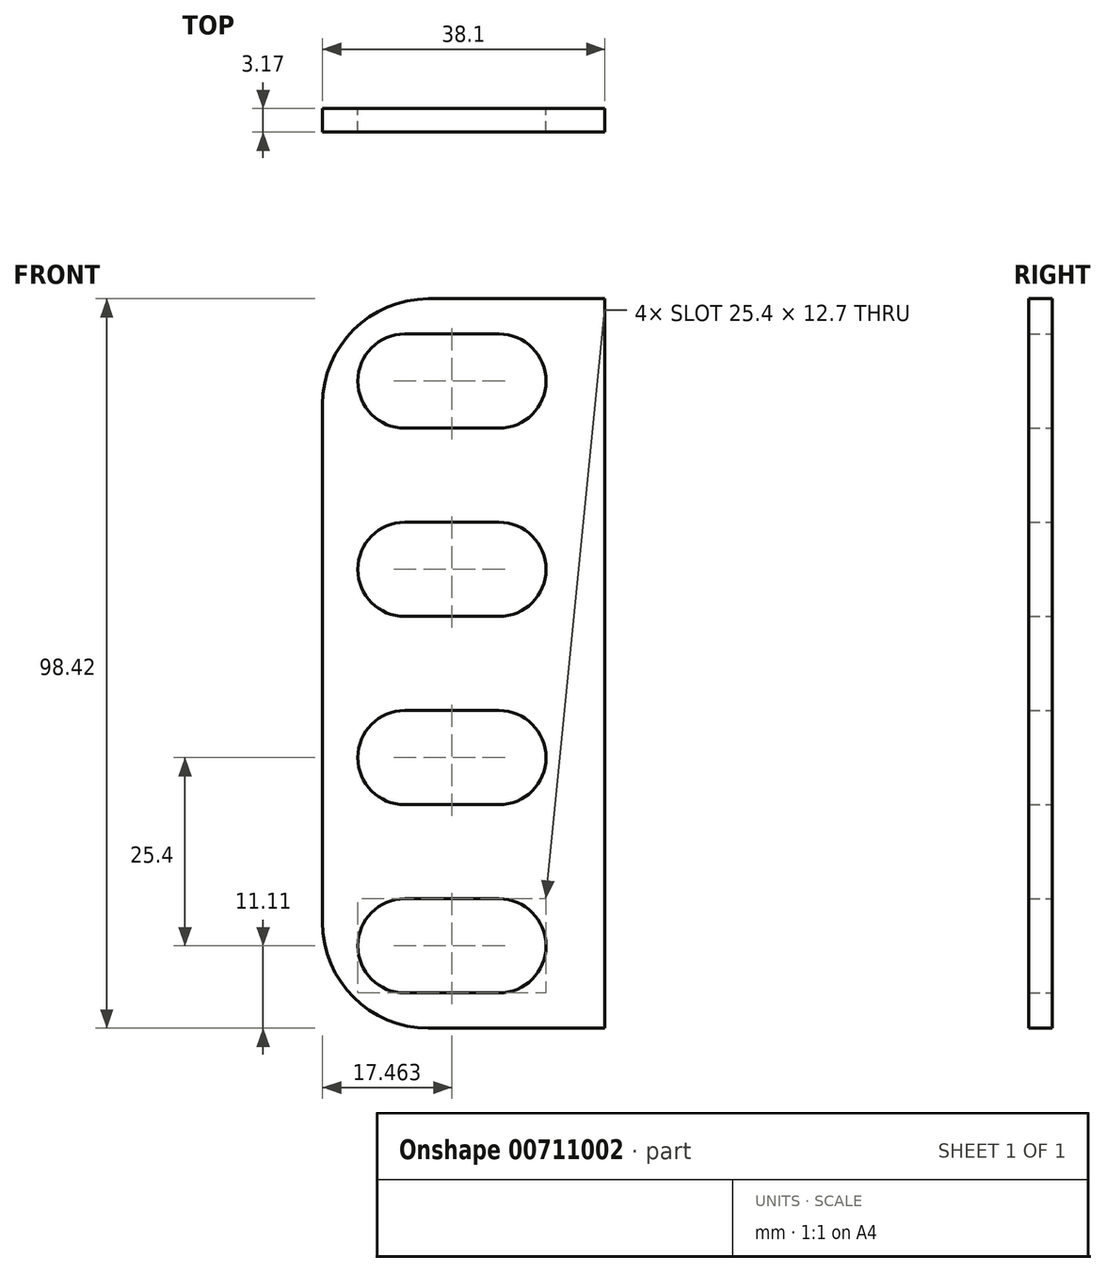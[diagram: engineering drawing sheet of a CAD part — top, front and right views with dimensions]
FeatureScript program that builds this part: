
annotation { "Feature Type Name" : "Feature", "Feature Type Description" : "" }
export const myFeature = defineFeature(function(context is Context, id is Id, definition is map)
    precondition{}
    {
        {
            var Q0;
            Q0=qCreatedBy(makeId("Front.planeOp"),FACE);
            var sketch = newSketch(context, id + "F0", { "sketchPlane" : qUnion([Q0])});
            skLineSegment(sketch, "E0.bottom", {"start": v(19.05, -49.21) * mm, "end": v(-4.76, -49.21) * mm});
            skLineSegment(sketch, "E0.top", {"start": v(19.05, 49.21) * mm, "end": v(-4.76, 49.21) * mm});
            skLineSegment(sketch, "E0.left", {"start": v(19.05, -49.21) * mm, "end": v(19.05, 49.21) * mm});
            skLineSegment(sketch, "E0.right", {"start": v(-19.05, -34.93) * mm, "end": v(-19.05, 34.92) * mm});
            skPoint(sketch, "E0.middle", {"position": v(0, 0) * mm});
            skPoint(sketch, "E1.visualSharp", {"position": v(-19.05, 49.21) * mm});
            skArc(sketch, "E1.filletArc", {"start": v(-4.76, 49.21) * mm, "mid": v(-14.87, 45.03) * mm, "end": v(-19.05, 34.92) * mm});
            skPoint(sketch, "E2.visualSharp", {"position": v(-19.05, -49.21) * mm});
            skArc(sketch, "E2.filletArc", {"start": v(-19.05, -34.93) * mm, "mid": v(-14.87, -45.03) * mm, "end": v(-4.76, -49.21) * mm});
            skLineSegment(sketch, "E3.bottom", {"start": v(4.76, -44.45) * mm, "end": v(-7.94, -44.45) * mm});
            skLineSegment(sketch, "E3.top", {"start": v(4.76, -31.75) * mm, "end": v(-7.94, -31.75) * mm});
            skLineSegment(sketch, "E3.left", {"start": v(11.11, -38.1) * mm, "end": v(11.11, -38.1) * mm});
            skLineSegment(sketch, "E3.right", {"start": v(-14.29, -38.1) * mm, "end": v(-14.29, -38.1) * mm});
            skPoint(sketch, "E4.visualSharp", {"position": v(-14.29, -31.75) * mm});
            skArc(sketch, "E4.filletArc", {"start": v(-7.94, -31.75) * mm, "mid": v(-12.43, -33.6) * mm, "end": v(-14.29, -38.1) * mm});
            skPoint(sketch, "E5.visualSharp", {"position": v(-14.29, -44.45) * mm});
            skArc(sketch, "E5.filletArc", {"start": v(-14.29, -38.1) * mm, "mid": v(-12.43, -42.6) * mm, "end": v(-7.94, -44.45) * mm});
            skPoint(sketch, "E6.visualSharp", {"position": v(11.11, -31.75) * mm});
            skArc(sketch, "E6.filletArc", {"start": v(11.11, -38.1) * mm, "mid": v(9.25, -33.6) * mm, "end": v(4.76, -31.75) * mm});
            skPoint(sketch, "E7.visualSharp", {"position": v(11.11, -44.45) * mm});
            skArc(sketch, "E7.filletArc", {"start": v(4.76, -44.45) * mm, "mid": v(9.25, -42.6) * mm, "end": v(11.11, -38.1) * mm});
            skLineSegment(sketch, "E8.0.1.0", {"start": v(4.76, -6.35) * mm, "end": v(-7.94, -6.35) * mm});
            skArc(sketch, "E8.0.1.1", {"start": v(11.11, -12.7) * mm, "mid": v(9.25, -8.2) * mm, "end": v(4.76, -6.35) * mm});
            skArc(sketch, "E8.0.1.2", {"start": v(-7.94, -6.35) * mm, "mid": v(-12.43, -8.2) * mm, "end": v(-14.29, -12.7) * mm});
            skArc(sketch, "E8.0.1.3", {"start": v(-14.29, -12.7) * mm, "mid": v(-12.43, -17.2) * mm, "end": v(-7.94, -19.05) * mm});
            skPoint(sketch, "E8.0.1.4", {"position": v(-14.29, -19.05) * mm});
            skLineSegment(sketch, "E8.0.1.5", {"start": v(4.76, -19.05) * mm, "end": v(-7.94, -19.05) * mm});
            skPoint(sketch, "E8.0.1.6", {"position": v(11.11, -6.35) * mm});
            skPoint(sketch, "E8.0.1.7", {"position": v(11.11, -19.05) * mm});
            skArc(sketch, "E8.0.1.8", {"start": v(4.76, -19.05) * mm, "mid": v(9.25, -17.2) * mm, "end": v(11.11, -12.7) * mm});
            skLineSegment(sketch, "E8.0.2.0", {"start": v(4.76, 19.05) * mm, "end": v(-7.94, 19.05) * mm});
            skArc(sketch, "E8.0.2.1", {"start": v(11.11, 12.7) * mm, "mid": v(9.25, 17.2) * mm, "end": v(4.76, 19.05) * mm});
            skArc(sketch, "E8.0.2.2", {"start": v(-7.94, 19.05) * mm, "mid": v(-12.43, 17.2) * mm, "end": v(-14.29, 12.7) * mm});
            skArc(sketch, "E8.0.2.3", {"start": v(-14.29, 12.7) * mm, "mid": v(-12.43, 8.2) * mm, "end": v(-7.94, 6.35) * mm});
            skPoint(sketch, "E8.0.2.4", {"position": v(-14.29, 6.35) * mm});
            skLineSegment(sketch, "E8.0.2.5", {"start": v(4.76, 6.35) * mm, "end": v(-7.94, 6.35) * mm});
            skPoint(sketch, "E8.0.2.6", {"position": v(11.11, 19.05) * mm});
            skPoint(sketch, "E8.0.2.7", {"position": v(11.11, 6.35) * mm});
            skArc(sketch, "E8.0.2.8", {"start": v(4.76, 6.35) * mm, "mid": v(9.25, 8.2) * mm, "end": v(11.11, 12.7) * mm});
            skLineSegment(sketch, "E8.0.3.0", {"start": v(4.76, 44.45) * mm, "end": v(-7.94, 44.45) * mm});
            skArc(sketch, "E8.0.3.1", {"start": v(11.11, 38.1) * mm, "mid": v(9.25, 42.6) * mm, "end": v(4.76, 44.45) * mm});
            skArc(sketch, "E8.0.3.2", {"start": v(-7.94, 44.45) * mm, "mid": v(-12.43, 42.6) * mm, "end": v(-14.29, 38.1) * mm});
            skArc(sketch, "E8.0.3.3", {"start": v(-14.29, 38.1) * mm, "mid": v(-12.43, 33.6) * mm, "end": v(-7.94, 31.75) * mm});
            skPoint(sketch, "E8.0.3.4", {"position": v(-14.29, 31.75) * mm});
            skLineSegment(sketch, "E8.0.3.5", {"start": v(4.76, 31.75) * mm, "end": v(-7.94, 31.75) * mm});
            skPoint(sketch, "E8.0.3.6", {"position": v(11.11, 44.45) * mm});
            skPoint(sketch, "E8.0.3.7", {"position": v(11.11, 31.75) * mm});
            skArc(sketch, "E8.0.3.8", {"start": v(4.76, 31.75) * mm, "mid": v(9.25, 33.6) * mm, "end": v(11.11, 38.1) * mm});
            skLineSegment(sketch, "E8.direction1", {"start": v(-14.29, -44.45) * mm, "end": v(12.7, -44.45) * mm, "construction": true});
            skLineSegment(sketch, "E8.direction2", {"start": v(-14.29, -44.45) * mm, "end": v(-14.29, -19.05) * mm, "construction": true});
            skSolve(sketch);
        }
        {
            var Q0;
            Q0 = qSketchRegion(id + "F0", true);
            extrude(context, id + "F1", {"entities" : qUnion([Q0]), "depth" : 3.17 * mm, "offsetDistance" : 25.4 * mm});
        }
    });
